# Revit family: Legrand_Hotel_UX_TOUCH_Commande_Tactile_Scenario
name_source: partatom
category: Equipement électrique
units: mm (PartAtom-declared; Revit-internal decimal feet)

## family parameters
Configuration du panneau = Deux colonnes, circuits au sein
Cote de connecteur circulaire = Utiliser le diamètre
Couper avec des vides une fois chargée = Non
Hôte = Face
Partagée = Non
Point de calcul de pièce = Non
Type d'élément = Tableau de raccordement

## types (3) — shared parameters
Adressable = Oui
Autres systèmes de bus = autre
Avec affichage LED = Oui
Classe de protection (IP) = IP20
Condition Générale d'Utilisation = https://export.legrand.com
Consommation en veille (mA) = 8
Couleur = noir
Elévation par défaut = 1300 mm  [stored 4.26509 ft]
Fabricant = Legrand
Finition de la surface = brillant
Fréquence d'alimentation MIN-MAX (Hz) = 0-0
Hauteur hors tout = 93 mm  [stored 0.305118 ft]
Largeur hors tout = 129 mm  [stored 0.423228 ft]
Matériau = LEGRAND - Plastique noir
Moyen de programmation = Ordinateur
Profondeur d'encastrement = 30 mm  [stored 0.0984252 ft]
Profondeur hors tout = 42 mm  [stored 0.137795 ft]
Programmable = Oui
Résistance aux chocs (IK) = IK02
Site web configurateur = https://uxforupscalehotel.legrand.com
Temperature d'utilisation /d'installation MIN-MAX (°C) = 0-40
Temperature de stockage MIN-MAX (°C) = -20-70
Type de montage = encastré
URL = http://www.legrandoc.com

## per-type parameters (varying)
| type | Avec thermostat d'ambiance | Commande | Description | Modèle | Nombre de touches |
| Thermostat_Commande Tête de Lit | Oui | Tête de lit | Commande tête de lit SCS | 048772 | 10 |
| 4 scénarios | Non | 4 touches | Commande tactile 4 touches | 048777 | 4 |
| 6 scénarios | Non | 6 touches | Commande tactile 6 touches | 048774 | 6 |

note: [stored X ft] marks values corroborated as IEEE doubles in the binary element streams (Revit-internal decimal feet)
